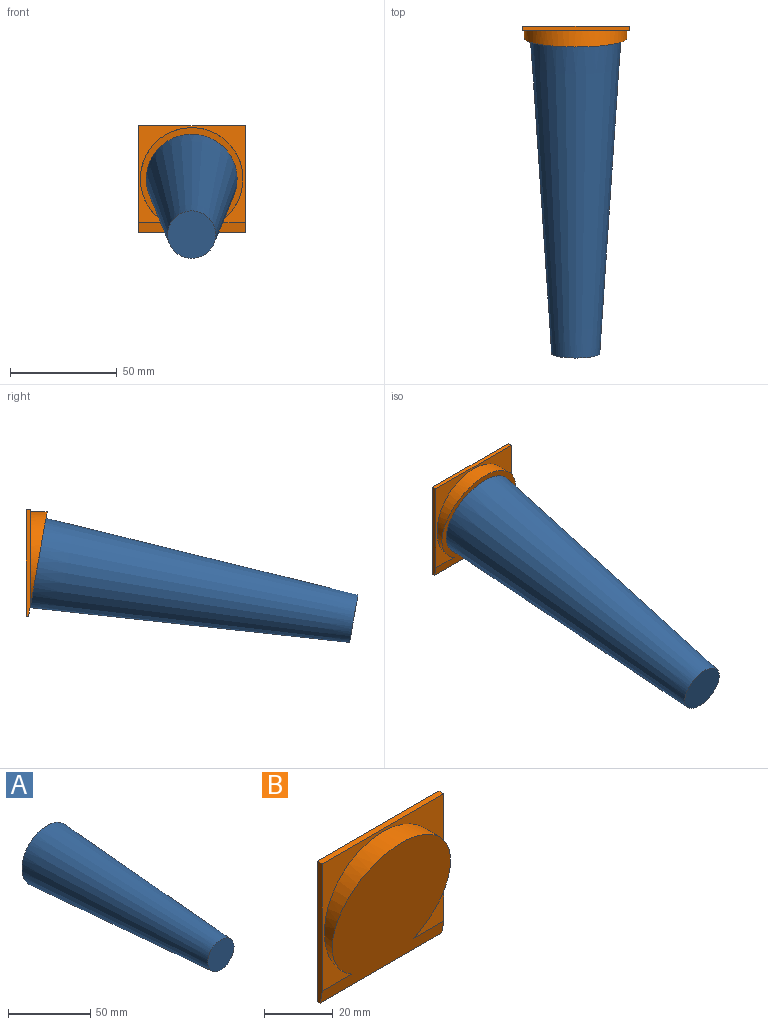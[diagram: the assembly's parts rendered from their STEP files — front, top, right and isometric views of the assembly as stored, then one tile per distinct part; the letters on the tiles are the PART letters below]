
ASSEMBLY  parts=2 mates=1
PART A: 3 faces, bbox 42.5x150x42.5 mm
  f0: cone r=21.25mm half-angle=3.8deg, axis (0,1,0), area 15366.5mm2, adj f1,f2
  f1: plane 22.57x22.57mm, normal (0,-1,0), area 400.2mm2, adj f0
  f2: plane 42.5x42.5mm, normal (0,1,0), area 1418.6mm2, adj f0
PART B: 8 faces, bbox 50x9.9x50 mm
  f0: plane 50x2mm, normal (0,0,1), area 100mm2, adj f1,f2,f5,f7
  f1: plane 50x2mm, normal (1,0,0), area 98.1mm2, adj f0,f3,f4,f5,f7
  f2: plane 50x2mm, normal (-1,0,0), area 98.1mm2, adj f0,f3,f4,f5,f7
  f3: plane 50x49.02mm, normal (0,-0.98,-0.17), area 2009.6mm2, adj f1,f2,f4,f6,f7
  f4: plane 50x1.18mm, normal (0,0,-1), area 59.2mm2, adj f1,f2,f3,f5
  f5: plane 50x50mm, normal (0,1,0), area 2500mm2, adj f0,f1,f2,f4
  f6: cylinder r=24mm len=48mm, axis (0,-1,0), area 553.4mm2, adj f3,f7
  f7: plane 50x45.37mm, normal (0,-1,0), area 520.9mm2, adj f0,f1,f2,f3,f6
PLACE A rot(axis=(1,0,0),10deg) t=(2.43,35.81,-55.83)mm
PLACE B t=(-41.16,41.4,-11.01)mm
MATE fastened A.f0 <-> B.f3  axis (0,0.98,0.17) through (2.43,35.81,-55.83)mm
